# Revit family: Shower-Handshower-KOHLER-Awaken-K-72415
name_source: partatom
category: Plumbing Fixtures
revit_build: Autodesk Revit 2015 (Build: 20140606_1530(x64)
units: mm (PartAtom-declared; Revit-internal decimal feet)

## types (4) — shared parameters
ADA Compliant = Yes
Assembly Code = D2010700
Date Modified = 09/23/2017
Default Elevation = 36"
Description = Awaken G110 2.0 gpm multifunction handshower
Flow Rate = 2 GPM
HW Connection = Yes
Height = 9 7/8"
Inlet Connector = Inlet Connection
Length = 3"
Manufacturer = Kohler
MasterFormat 1995 = 15410
MasterFormat 2004 = 22.41.23
Material = Premium Metal Construction
Outlet Connector = Outlet Connection
Pressure = 0.00 psi
Product Documentation Link = http://www.us.kohler.com
Product Name = Awaken
Product Page URL = http://www.us.kohler.com
URL = http://www.us.kohler.com
Width = 4 5/16"

## per-type parameters (varying)
| type | Finish | Model | Type | Waste Connection |
| CP-Polished Chrome | Kohler-Metal-CP-Polished_Chrome | K-72415-CP | 1 | No |
| BN-Vibrant Brushed Nickel | Kohler-Metal-BN-Vibrant_Brushed_Nickel | K-72415-BN | 2 | Yes |
| 2BZ-Oil Rubbed Bronze | Kohler-Metal-2BZ-Oil_Rubbed_Bronze | K-72415-2BZ | 3 | Yes |
| BL-Matte Black | Kohler-Metal-BL-Matte_Black | K-72415-BL | 4 | Yes |

## geometry (parser evidence)
native form markers: Blend x4, Sweep x5
no freeform markers — native parametric forms only
